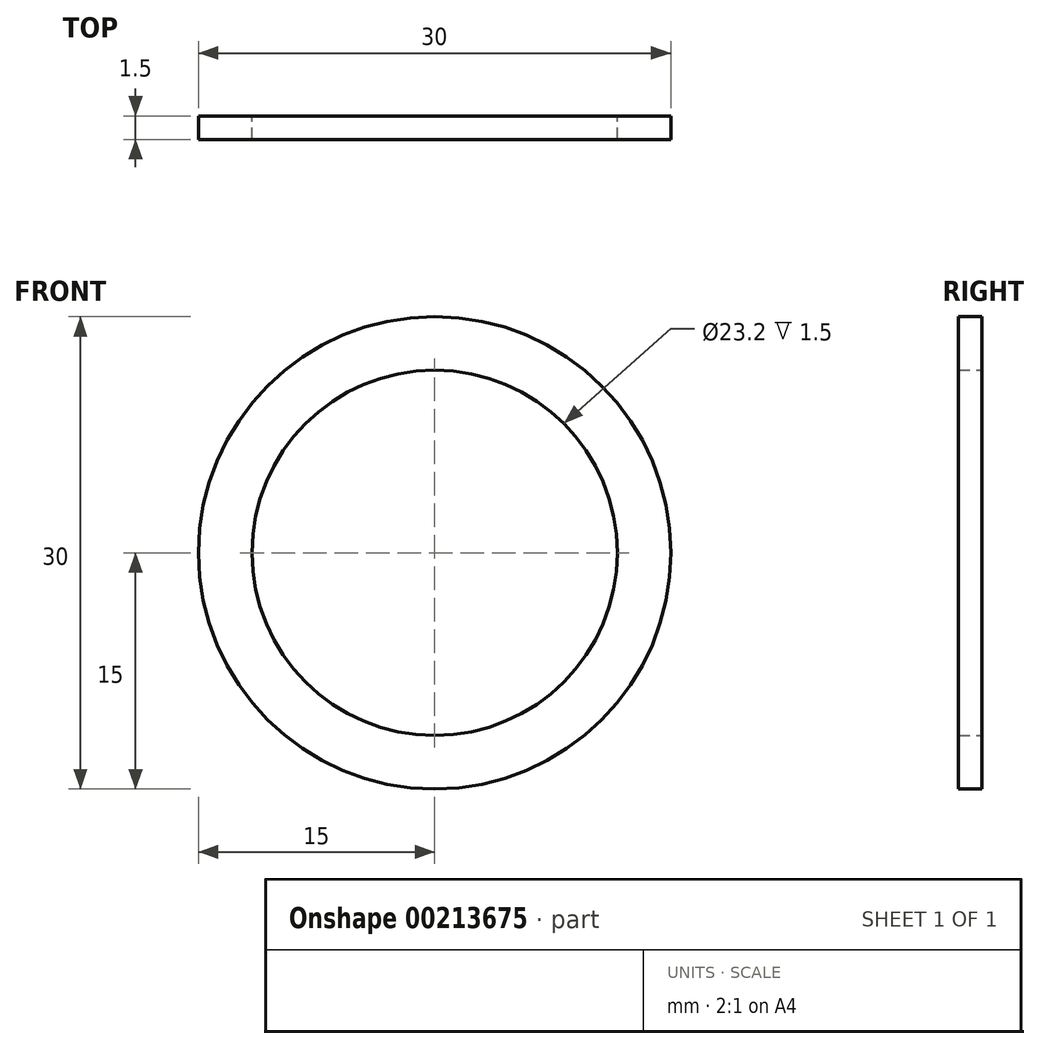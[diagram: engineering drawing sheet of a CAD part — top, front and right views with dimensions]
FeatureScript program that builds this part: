
annotation { "Feature Type Name" : "Feature", "Feature Type Description" : "" }
export const myFeature = defineFeature(function(context is Context, id is Id, definition is map)
    precondition{}
    {
        {
            var Q0;
            Q0=qCreatedBy(makeId("Front.planeOp"),FACE);
            var sketch = newSketch(context, id + "F0", { "sketchPlane" : qUnion([Q0])});
            skCircle(sketch, "E0", {"center": v(0, 0) * mm, "radius": 15 * mm});
            skCircle(sketch, "E1", {"center": v(0, 0) * mm, "radius": 11.6 * mm});
            skSolve(sketch);
        }
        {
            var Q0;
            Q0=makeQuery(id+"F0.imprint","IMPRINT",FACE,{"disambiguationData":[TD([[makeQuery(id+"F0.imprint","IMPRINT",EDGE,{"derivedFrom":sQuery(id+"F0.wireOp",EDGE,"E0")}),1.0]])]});
            extrude(context, id + "F1", {"entities" : qUnion([Q0]), "depth" : 1.5 * mm});
        }
    });
